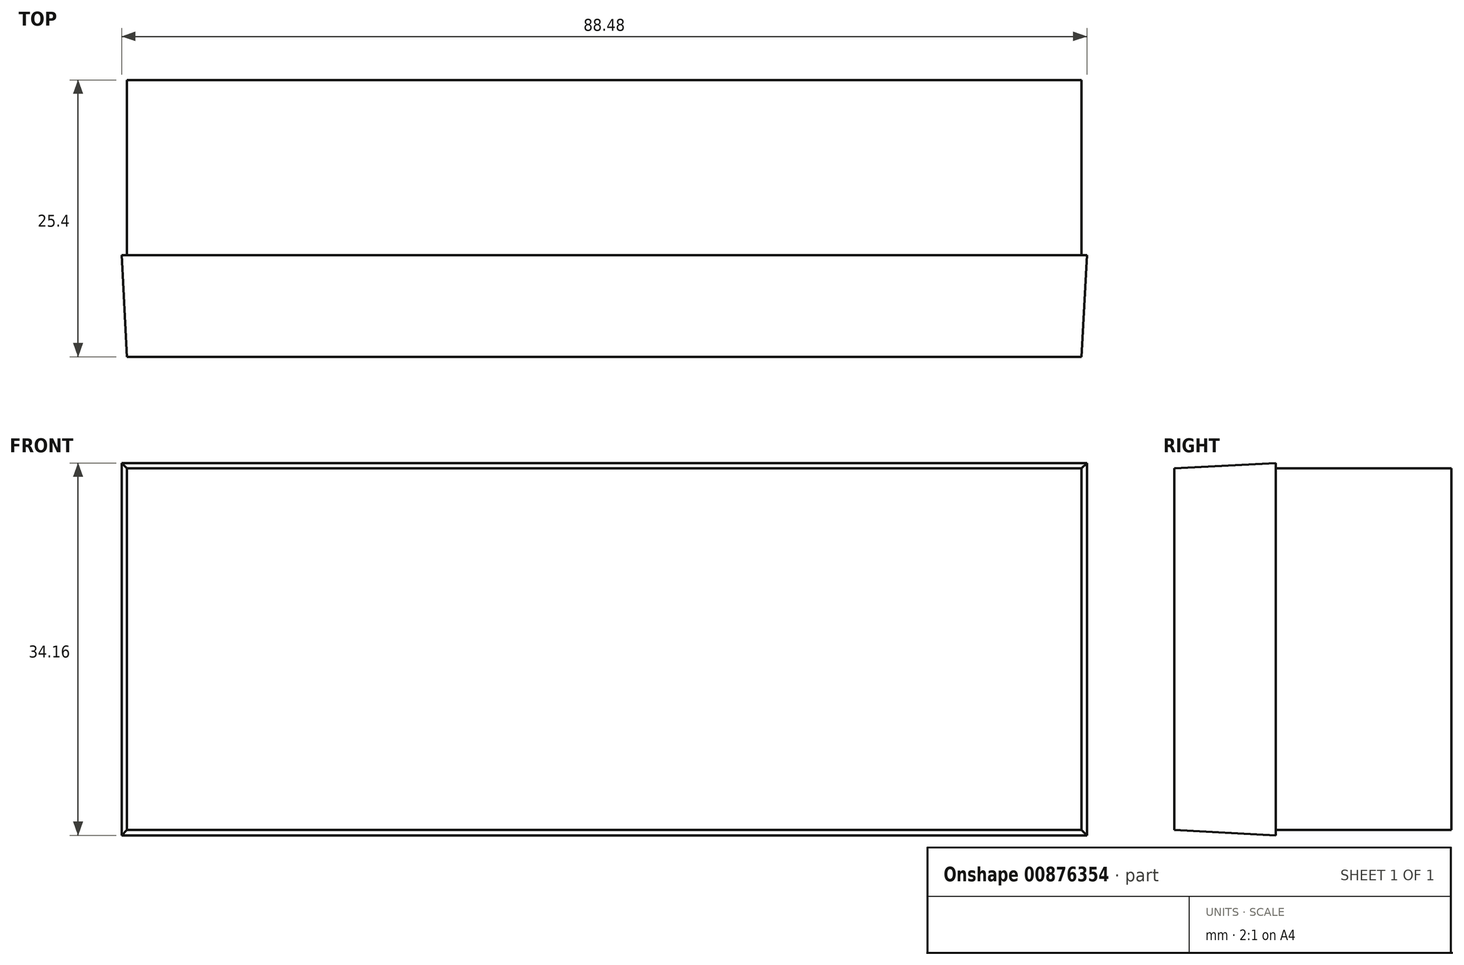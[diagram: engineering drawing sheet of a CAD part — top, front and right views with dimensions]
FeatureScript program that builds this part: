
annotation { "Feature Type Name" : "Feature", "Feature Type Description" : "" }
export const myFeature = defineFeature(function(context is Context, id is Id, definition is map)
    precondition{}
    {
        {
            var Q0;
            Q0=qCreatedBy(makeId("Front.planeOp"),FACE);
            var sketch = newSketch(context, id + "F0", { "sketchPlane" : qUnion([Q0])});
            skLineSegment(sketch, "E0.bottom", {"start": v(43.75, -16.6) * mm, "end": v(-43.75, -16.6) * mm});
            skLineSegment(sketch, "E0.top", {"start": v(43.75, 16.6) * mm, "end": v(-43.75, 16.6) * mm});
            skLineSegment(sketch, "E0.left", {"start": v(43.75, -16.6) * mm, "end": v(43.75, 16.6) * mm});
            skLineSegment(sketch, "E0.right", {"start": v(-43.75, -16.6) * mm, "end": v(-43.75, 16.6) * mm});
            skPoint(sketch, "E0.middle", {"position": v(0, 0) * mm});
            skSolve(sketch);
        }
        {
            var Q0;
            Q0 = qSketchRegion(id + "F0", true);
            extrude(context, id + "F1", {"entities" : qUnion([Q0]), "depth" : 25.4 * mm, "offsetDistance" : 25.4 * mm});
        }
        {
            var Q0;
            Q0=makeQuery(id+"F1.opExtrude","CAP_FACE",FACE,{"disambiguationData":[OSD([sQuery(id+"F0.wireOp",EDGE,"E0.bottom"),sQuery(id+"F0.wireOp",EDGE,"E0.top"),sQuery(id+"F0.wireOp",EDGE,"E0.left"),sQuery(id+"F0.wireOp",EDGE,"E0.right")])],"isStart":false});
            extrude(context, id + "F2", {"entities" : qUnion([Q0]), "operationType" : NewBodyOperationType.ADD, "oppositeDirection" : true, "depth" : 9.32 * mm, "offsetDistance" : 25.4 * mm, "hasDraft" : true, "draftAngle" : 3 * degree});
        }
    });
